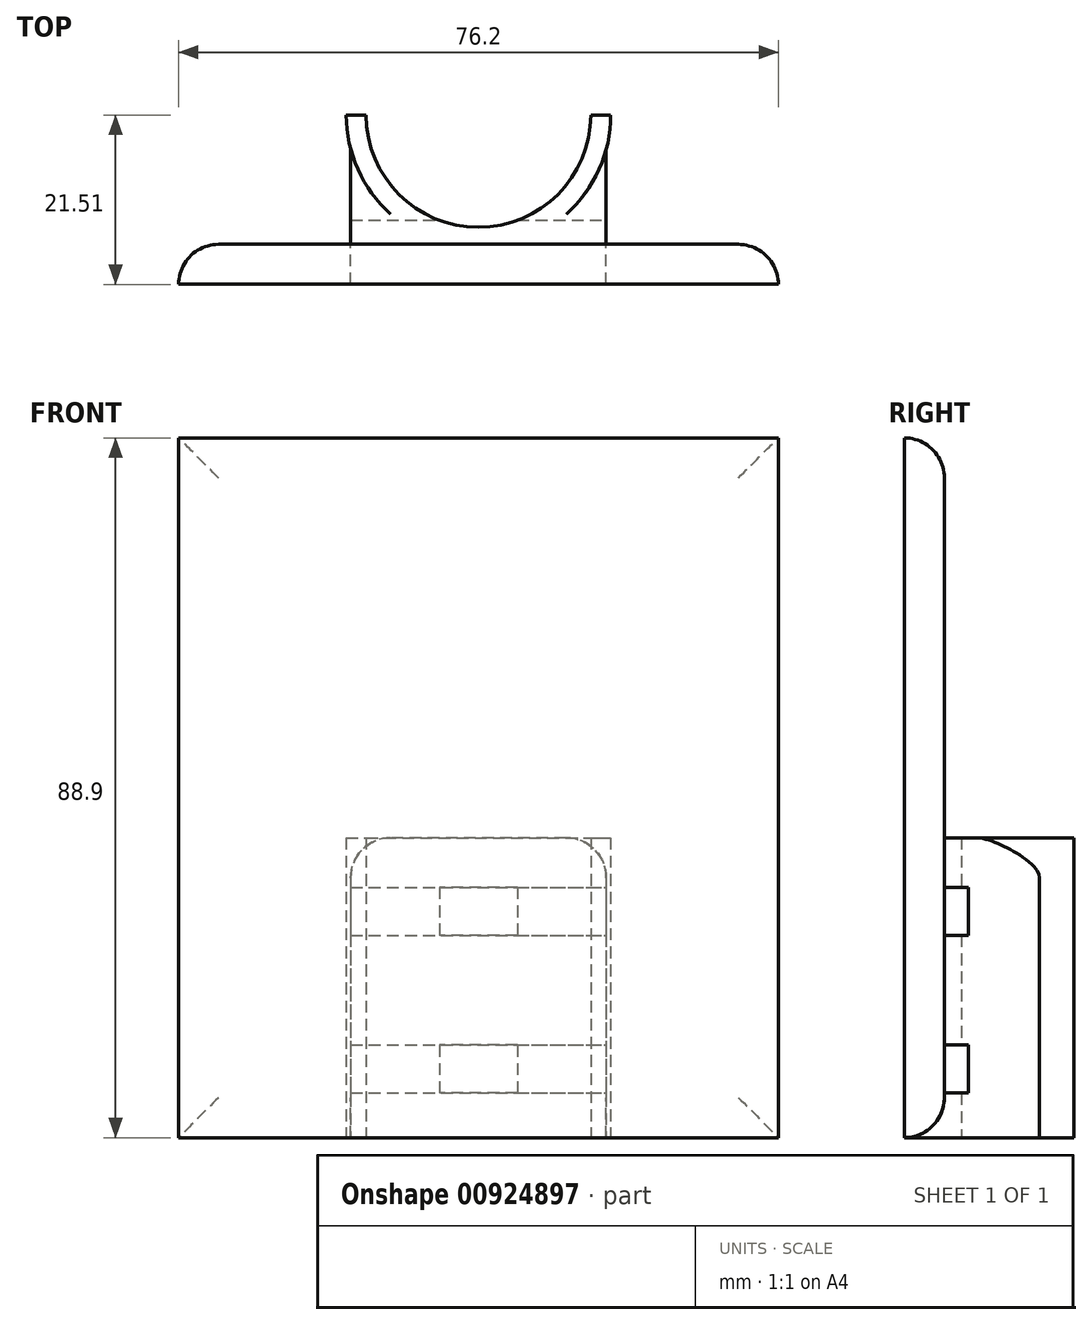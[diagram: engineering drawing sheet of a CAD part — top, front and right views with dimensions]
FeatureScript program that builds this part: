
annotation { "Feature Type Name" : "Feature", "Feature Type Description" : "" }
export const myFeature = defineFeature(function(context is Context, id is Id, definition is map)
    precondition{}
    {
        {
            var Q0;
            Q0=qCreatedBy(makeId("Top.planeOp"),FACE);
            var sketch = newSketch(context, id + "F0", { "sketchPlane" : qUnion([Q0])});
            skArc(sketch, "E0", {"start": v(-14.27, 0) * mm, "mid": v(0, -14.27) * mm, "end": v(14.27, 0) * mm});
            skPoint(sketch, "E1.left.start.orphan", {"position": v(0, -14.27) * mm});
            skArc(sketch, "E2", {"start": v(-16.8, 0) * mm, "mid": v(-16.66, -2.2) * mm, "end": v(-16.23, -4.34) * mm});
            skLineSegment(sketch, "E3", {"start": v(-16.8, 0) * mm, "end": v(-14.27, 0) * mm});
            skLineSegment(sketch, "E4", {"start": v(14.27, 0) * mm, "end": v(16.8, 0) * mm});
            skLineSegment(sketch, "E5.bottom", {"start": v(38.1, -21.5) * mm, "end": v(-38.1, -21.5) * mm});
            skLineSegment(sketch, "E5.top", {"start": v(38.1, -16.43) * mm, "end": v(3.53, -16.43) * mm});
            skLineSegment(sketch, "E5.left", {"start": v(38.1, -21.5) * mm, "end": v(38.1, -16.43) * mm});
            skLineSegment(sketch, "E5.right", {"start": v(-38.1, -21.5) * mm, "end": v(-38.1, -16.43) * mm});
            skPoint(sketch, "E5.middle", {"position": v(0, -18.97) * mm});
            skLineSegment(sketch, "E6.trimOffspring", {"start": v(-3.53, -16.43) * mm, "end": v(-38.1, -16.43) * mm});
            skLineSegment(sketch, "E7", {"start": v(-16.23, -4.34) * mm, "end": v(-16.23, -16.43) * mm});
            skLineSegment(sketch, "E8", {"start": v(16.23, -4.34) * mm, "end": v(16.23, -16.43) * mm});
            skArc(sketch, "E9.trimOffspring", {"start": v(16.23, -4.34) * mm, "mid": v(16.66, -2.2) * mm, "end": v(16.8, 0) * mm});
            skLineSegment(sketch, "E10", {"start": v(-3.53, -16.43) * mm, "end": v(3.53, -16.43) * mm});
            skSolve(sketch);
        }
        {
            var Q0;
            Q0=makeQuery(id+"F0.imprint","IMPRINT",FACE,{"disambiguationData":[TD([[makeQuery(id+"F0.imprint","IMPRINT",EDGE,{"derivedFrom":sQuery(id+"F0.wireOp",EDGE,"E5.bottom")}),-1.0]])]});
            extrude(context, id + "F1", {"entities" : qUnion([Q0]), "depth" : 88.9 * mm, "offsetDistance" : 25.4 * mm});
        }
        {
            var Q0;
            Q0=makeQuery(id+"F0.imprint","IMPRINT",FACE,{"disambiguationData":[TD([[makeQuery(id+"F0.imprint","IMPRINT",EDGE,{"derivedFrom":sQuery(id+"F0.wireOp",EDGE,"E0")}),-1.0]])]});
            extrude(context, id + "F2", {"entities" : qUnion([Q0]), "operationType" : NewBodyOperationType.ADD, "depth" : 38.1 * mm, "offsetDistance" : 25.4 * mm});
        }
        {
            var Q0;
            Q0=makeQuery(id+"F1.opExtrude","SWEPT_FACE",FACE,{"disambiguationData":[OSD([sQuery(id+"F0.wireOp",EDGE,"E5.left")])]});
            var sketch = newSketch(context, id + "F3", { "sketchPlane" : qUnion([Q0])});
            skLineSegment(sketch, "E11.bottom", {"start": v(-16.43, 31.8) * mm, "end": v(-13.38, 31.8) * mm});
            skLineSegment(sketch, "E11.top", {"start": v(-16.43, 25.7) * mm, "end": v(-13.38, 25.7) * mm});
            skLineSegment(sketch, "E11.left", {"start": v(-16.43, 31.8) * mm, "end": v(-16.43, 25.7) * mm});
            skLineSegment(sketch, "E11.right", {"start": v(-13.38, 31.8) * mm, "end": v(-13.38, 25.7) * mm});
            skPoint(sketch, "E12.oppositeSnap0", {"position": v(-13.38, 28.75) * mm});
            skLineSegment(sketch, "E12.bottom", {"start": v(-16.43, 11.77) * mm, "end": v(-13.38, 11.77) * mm});
            skLineSegment(sketch, "E12.top", {"start": v(-16.43, 5.67) * mm, "end": v(-13.38, 5.67) * mm});
            skLineSegment(sketch, "E12.left", {"start": v(-16.43, 11.77) * mm, "end": v(-16.43, 5.67) * mm});
            skLineSegment(sketch, "E12.right", {"start": v(-13.38, 11.77) * mm, "end": v(-13.38, 5.67) * mm});
            skSolve(sketch);
        }
        {
            var Q0;
            Q0=makeQuery(id+"F3.imprint","IMPRINT",FACE,{"disambiguationData":[TD([[makeQuery(id+"F3.imprint","IMPRINT",EDGE,{"derivedFrom":sQuery(id+"F3.wireOp",EDGE,"E12.bottom")}),-1.0]])]});
            var Q1;
            Q1=makeQuery(id+"F3.imprint","IMPRINT",FACE,{"disambiguationData":[TD([[makeQuery(id+"F3.imprint","IMPRINT",EDGE,{"derivedFrom":sQuery(id+"F3.wireOp",EDGE,"E11.bottom")}),-1.0]])]});
            extrude(context, id + "F4", {"entities" : qUnion([Q0, Q1]), "operationType" : NewBodyOperationType.REMOVE, "endBound" : BoundingType.THROUGH_ALL, "oppositeDirection" : true, "depth" : 25.4 * mm, "offsetDistance" : 25.4 * mm});
        }
        {
            var Q0;
            Q0=makeQuery(id+"F1.opExtrude","CAP_EDGE",EDGE,{"disambiguationData":[OSD([sQuery(id+"F0.wireOp",EDGE,"E5.top"),sQuery(id+"F0.wireOp",EDGE,"E6.trimOffspring"),sQuery(id+"F0.wireOp",EDGE,"E10")])],"isStart":false});
            var Q1;
            Q1=makeQuery(id+"F1.opExtrude","SWEPT_EDGE",EDGE,{"disambiguationData":[OSD([sQuery(id+"F0.wireOp",EDGE,"E5.top"),sQuery(id+"F0.wireOp",EDGE,"E5.left")])]});
            var Q2;
            Q2=makeQuery(id+"F4.boolean.opBoolean","INTERSECT",EDGE,{"derivedFrom":[makeQuery(id+"F4.opExtrude","SWEPT_FACE",FACE,{"disambiguationData":[OSD([sQuery(id+"F3.wireOp",EDGE,"E11.left")])]}),makeQuery(id+"F4.opExtrude","SWEPT_FACE",FACE,{"disambiguationData":[OSD([sQuery(id+"F3.wireOp",EDGE,"E12.left")])]})]});
            var Q3;
            {var subQ0=sQuery(id+"F0.wireOp",EDGE,"E10");var subQ2=sQuery(id+"F0.wireOp",EDGE,"E6.trimOffspring");var subQ3=sQuery(id+"F0.wireOp",EDGE,"E5.top");var subQ4=sQuery(id+"F0.wireOp",EDGE,"E5.left");Q3=makeQuery(id+"F2.boolean.opBoolean","SPLIT",EDGE,{"disambiguationData":[TD([makeQuery(id+"F1.opExtrude","SWEPT_FACE",FACE,{"disambiguationData":[OSD([subQ4])]})])],"derivedFrom":makeQuery(id+"F1.opExtrude","CAP_EDGE",EDGE,{"disambiguationData":[OSD([subQ3,subQ2,subQ0])],"isStart":true})});}
            var Q4;
            {var subQ0=sQuery(id+"F0.wireOp",EDGE,"E10");var subQ2=sQuery(id+"F0.wireOp",EDGE,"E6.trimOffspring");var subQ3=sQuery(id+"F0.wireOp",EDGE,"E5.top");var subQ4=sQuery(id+"F0.wireOp",EDGE,"E5.right");Q4=makeQuery(id+"F2.boolean.opBoolean","SPLIT",EDGE,{"disambiguationData":[TD([makeQuery(id+"F1.opExtrude","SWEPT_FACE",FACE,{"disambiguationData":[OSD([subQ4])]})])],"derivedFrom":makeQuery(id+"F1.opExtrude","CAP_EDGE",EDGE,{"disambiguationData":[OSD([subQ3,subQ2,subQ0])],"isStart":true})});}
            var Q5;
            Q5=makeQuery(id+"F2.opExtrude","CAP_EDGE",EDGE,{"disambiguationData":[OSD([sQuery(id+"F0.wireOp",EDGE,"E8")])],"isStart":false});
            var Q6;
            Q6=makeQuery(id+"F2.opExtrude","CAP_EDGE",EDGE,{"disambiguationData":[OSD([sQuery(id+"F0.wireOp",EDGE,"E7")])],"isStart":false});
            fillet(context, id + "F5", {"entities" : qUnion([Q0, Q1, Q2, Q3, Q4, Q5, Q6]), "radius" : 5.08 * mm, "tangentPropagation" : true, "allowEdgeOverflow" : false});
        }
    });
